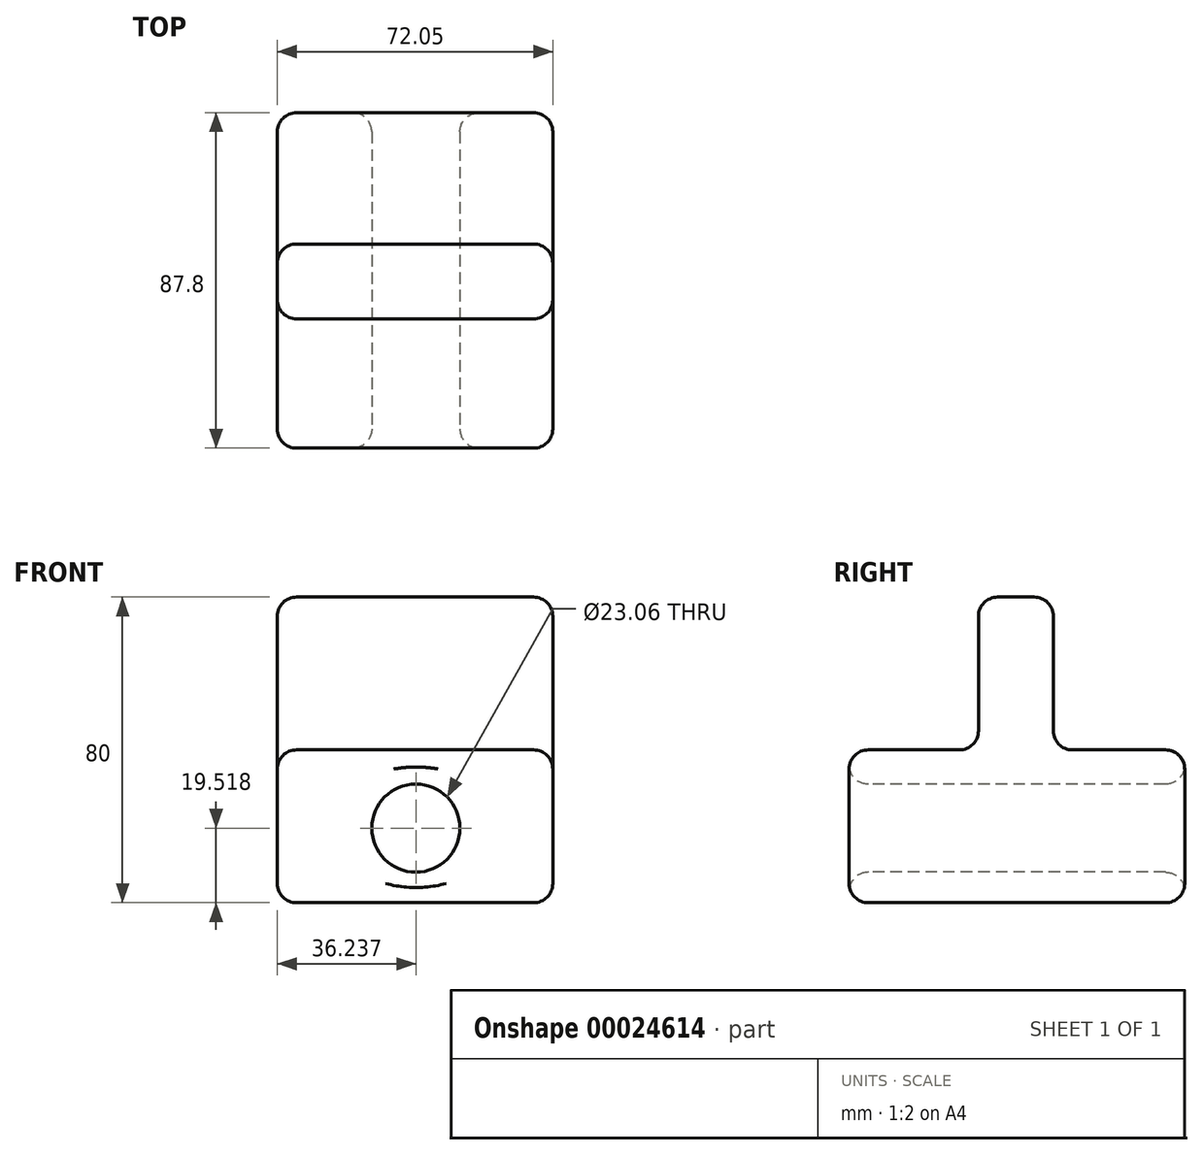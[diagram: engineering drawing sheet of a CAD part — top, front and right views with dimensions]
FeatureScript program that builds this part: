
annotation { "Feature Type Name" : "Feature", "Feature Type Description" : "" }
export const myFeature = defineFeature(function(context is Context, id is Id, definition is map)
    precondition{}
    {
        {
            var Q0;
            Q0=qCreatedBy(makeId("Top.planeOp"),FACE);
            var sketch = newSketch(context, id + "F0", { "sketchPlane" : qUnion([Q0])});
            skLineSegment(sketch, "E0.bottom", {"start": v(-59.89, -44.54) * mm, "end": v(12.16, -44.54) * mm});
            skLineSegment(sketch, "E0.top", {"start": v(-59.89, 43.26) * mm, "end": v(12.16, 43.26) * mm});
            skLineSegment(sketch, "E0.left", {"start": v(-59.89, -44.54) * mm, "end": v(-59.89, 43.26) * mm});
            skLineSegment(sketch, "E0.right", {"start": v(12.16, -44.54) * mm, "end": v(12.16, 43.26) * mm});
            skSolve(sketch);
        }
        {
            var Q0;
            Q0=makeQuery(id+"F0.imprint","IMPRINT",FACE,{"disambiguationData":[TD([[makeQuery(id+"F0.imprint","IMPRINT",EDGE,{"derivedFrom":sQuery(id+"F0.wireOp",EDGE,"E0.bottom")}),1.0]])]});
            extrude(context, id + "F1", {"entities" : qUnion([Q0]), "depth" : 40 * mm});
        }
        {
            var Q0;
            Q0=makeQuery(id+"F1.opExtrude","SWEPT_FACE",FACE,{"disambiguationData":[OSD([sQuery(id+"F0.wireOp",EDGE,"E0.bottom")])]});
            var sketch = newSketch(context, id + "F2", { "sketchPlane" : qUnion([Q0])});
            skCircle(sketch, "E1", {"center": v(-23.65, 19.52) * mm, "radius": 11.53 * mm});
            skSolve(sketch);
        }
        {
            var Q0;
            Q0=makeQuery(id+"F2.imprint","IMPRINT",FACE,{"disambiguationData":[TD([[makeQuery(id+"F2.imprint","IMPRINT",EDGE,{"derivedFrom":sQuery(id+"F2.wireOp",EDGE,"E1")}),1.0]])]});
            extrude(context, id + "F3", {"entities" : qUnion([Q0]), "operationType" : NewBodyOperationType.REMOVE, "endBound" : BoundingType.THROUGH_ALL, "oppositeDirection" : true, "depth" : 25 * mm});
        }
        {
            var Q0;
            Q0=makeQuery(id+"F1.opExtrude","CAP_FACE",FACE,{"disambiguationData":[OSD([sQuery(id+"F0.wireOp",EDGE,"E0.bottom"),sQuery(id+"F0.wireOp",EDGE,"E0.top"),sQuery(id+"F0.wireOp",EDGE,"E0.left"),sQuery(id+"F0.wireOp",EDGE,"E0.right")])],"isStart":false});
            var sketch = newSketch(context, id + "F4", { "sketchPlane" : qUnion([Q0])});
            skLineSegment(sketch, "E2.bottom", {"start": v(-59.89, -10.7) * mm, "end": v(12.16, -10.7) * mm});
            skLineSegment(sketch, "E2.top", {"start": v(-59.89, 8.88) * mm, "end": v(12.16, 8.88) * mm});
            skLineSegment(sketch, "E2.left", {"start": v(-59.89, -10.7) * mm, "end": v(-59.89, 8.88) * mm});
            skLineSegment(sketch, "E2.right", {"start": v(12.16, -10.7) * mm, "end": v(12.16, 8.88) * mm});
            skSolve(sketch);
        }
        {
            var Q0;
            Q0=makeQuery(id+"F4.imprint","IMPRINT",FACE,{"disambiguationData":[TD([[makeQuery(id+"F4.imprint","IMPRINT",EDGE,{"derivedFrom":sQuery(id+"F4.wireOp",EDGE,"E2.bottom")}),1.0]])]});
            extrude(context, id + "F5", {"entities" : qUnion([Q0]), "operationType" : NewBodyOperationType.ADD, "depth" : 40 * mm});
        }
        {
            var Q0;
            {var subQ0=sQuery(id+"F0.wireOp",EDGE,"E0.right");var subQ1=sQuery(id+"F0.wireOp",EDGE,"E0.bottom");Q0=makeQuery(id+"F5.boolean.opBoolean","SPLIT",EDGE,{"disambiguationData":[TD([makeQuery(id+"F1.opExtrude","SWEPT_FACE",FACE,{"disambiguationData":[OSD([subQ1])]})])],"derivedFrom":makeQuery(id+"F1.opExtrude","CAP_EDGE",EDGE,{"disambiguationData":[OSD([subQ0])],"isStart":false})});}
            var Q1;
            {var subQ0=sQuery(id+"F0.wireOp",EDGE,"E0.bottom");var subQ1=sQuery(id+"F0.wireOp",EDGE,"E0.left");var subQ2=sQuery(id+"F0.wireOp",EDGE,"E0.right");Q1=makeQuery(id+"F5.boolean.opBoolean","SPLIT",FACE,{"disambiguationData":[TD([makeQuery(id+"F1.opExtrude","SWEPT_FACE",FACE,{"disambiguationData":[OSD([subQ0])]})])],"derivedFrom":makeQuery(id+"F1.opExtrude","CAP_FACE",FACE,{"disambiguationData":[OSD([subQ0,sQuery(id+"F0.wireOp",EDGE,"E0.top"),subQ1,subQ2])],"isStart":false})});}
            var Q2;
            {var subQ0=sQuery(id+"F0.wireOp",EDGE,"E0.top");var subQ1=sQuery(id+"F0.wireOp",EDGE,"E0.left");var subQ2=sQuery(id+"F0.wireOp",EDGE,"E0.right");Q2=makeQuery(id+"F5.boolean.opBoolean","SPLIT",FACE,{"disambiguationData":[TD([makeQuery(id+"F1.opExtrude","SWEPT_FACE",FACE,{"disambiguationData":[OSD([subQ0])]})])],"derivedFrom":makeQuery(id+"F1.opExtrude","CAP_FACE",FACE,{"disambiguationData":[OSD([sQuery(id+"F0.wireOp",EDGE,"E0.bottom"),subQ0,subQ1,subQ2])],"isStart":false})});}
            var Q3;
            Q3=makeQuery(id+"F5.opExtrude","CAP_FACE",FACE,{"disambiguationData":[OSD([sQuery(id+"F4.wireOp",EDGE,"E2.bottom"),sQuery(id+"F4.wireOp",EDGE,"E2.top"),sQuery(id+"F4.wireOp",EDGE,"E2.left"),sQuery(id+"F4.wireOp",EDGE,"E2.right")])],"isStart":false});
            var Q4;
            Q4=makeQuery(id+"F1.opExtrude","SWEPT_EDGE",EDGE,{"disambiguationData":[OSD([sQuery(id+"F0.wireOp",EDGE,"E0.bottom"),sQuery(id+"F0.wireOp",EDGE,"E0.left")])]});
            var Q5;
            Q5=makeQuery(id+"F3.boolean.opBoolean","COPY",EDGE,{"derivedFrom":makeQuery(id+"F3.opExtrude","CAP_EDGE",EDGE,{"disambiguationData":[OSD([sQuery(id+"F2.wireOp",EDGE,"E1")])],"isStart":true})});
            var Q6;
            Q6=makeQuery(id+"F1.opExtrude","SWEPT_FACE",FACE,{"disambiguationData":[OSD([sQuery(id+"F0.wireOp",EDGE,"E0.bottom")])]});
            var Q7;
            Q7=makeQuery(id+"F5.boolean.opBoolean","MERGE",FACE,{"derivedFrom":[makeQuery(id+"F1.opExtrude","SWEPT_FACE",FACE,{"disambiguationData":[OSD([sQuery(id+"F0.wireOp",EDGE,"E0.left")])]}),makeQuery(id+"F5.opExtrude","SWEPT_FACE",FACE,{"disambiguationData":[OSD([sQuery(id+"F4.wireOp",EDGE,"E2.left")])]})]});
            var Q8;
            Q8=makeQuery(id+"F1.opExtrude","SWEPT_FACE",FACE,{"disambiguationData":[OSD([sQuery(id+"F0.wireOp",EDGE,"E0.top")])]});
            var Q9;
            Q9=makeQuery(id+"F5.boolean.opBoolean","MERGE",FACE,{"derivedFrom":[makeQuery(id+"F1.opExtrude","SWEPT_FACE",FACE,{"disambiguationData":[OSD([sQuery(id+"F0.wireOp",EDGE,"E0.right")])]}),makeQuery(id+"F5.opExtrude","SWEPT_FACE",FACE,{"disambiguationData":[OSD([sQuery(id+"F4.wireOp",EDGE,"E2.right")])]})]});
            var Q10;
            Q10=makeQuery(id+"F1.opExtrude","CAP_FACE",FACE,{"disambiguationData":[OSD([sQuery(id+"F0.wireOp",EDGE,"E0.bottom"),sQuery(id+"F0.wireOp",EDGE,"E0.top"),sQuery(id+"F0.wireOp",EDGE,"E0.left"),sQuery(id+"F0.wireOp",EDGE,"E0.right")])],"isStart":true});
            fillet(context, id + "F6", {"entities" : qUnion([Q0, Q1, Q2, Q3, Q4, Q5, Q6, Q7, Q8, Q9, Q10]), "radius" : 5 * mm, "tangentPropagation" : true, "allowEdgeOverflow" : false});
        }
    });
